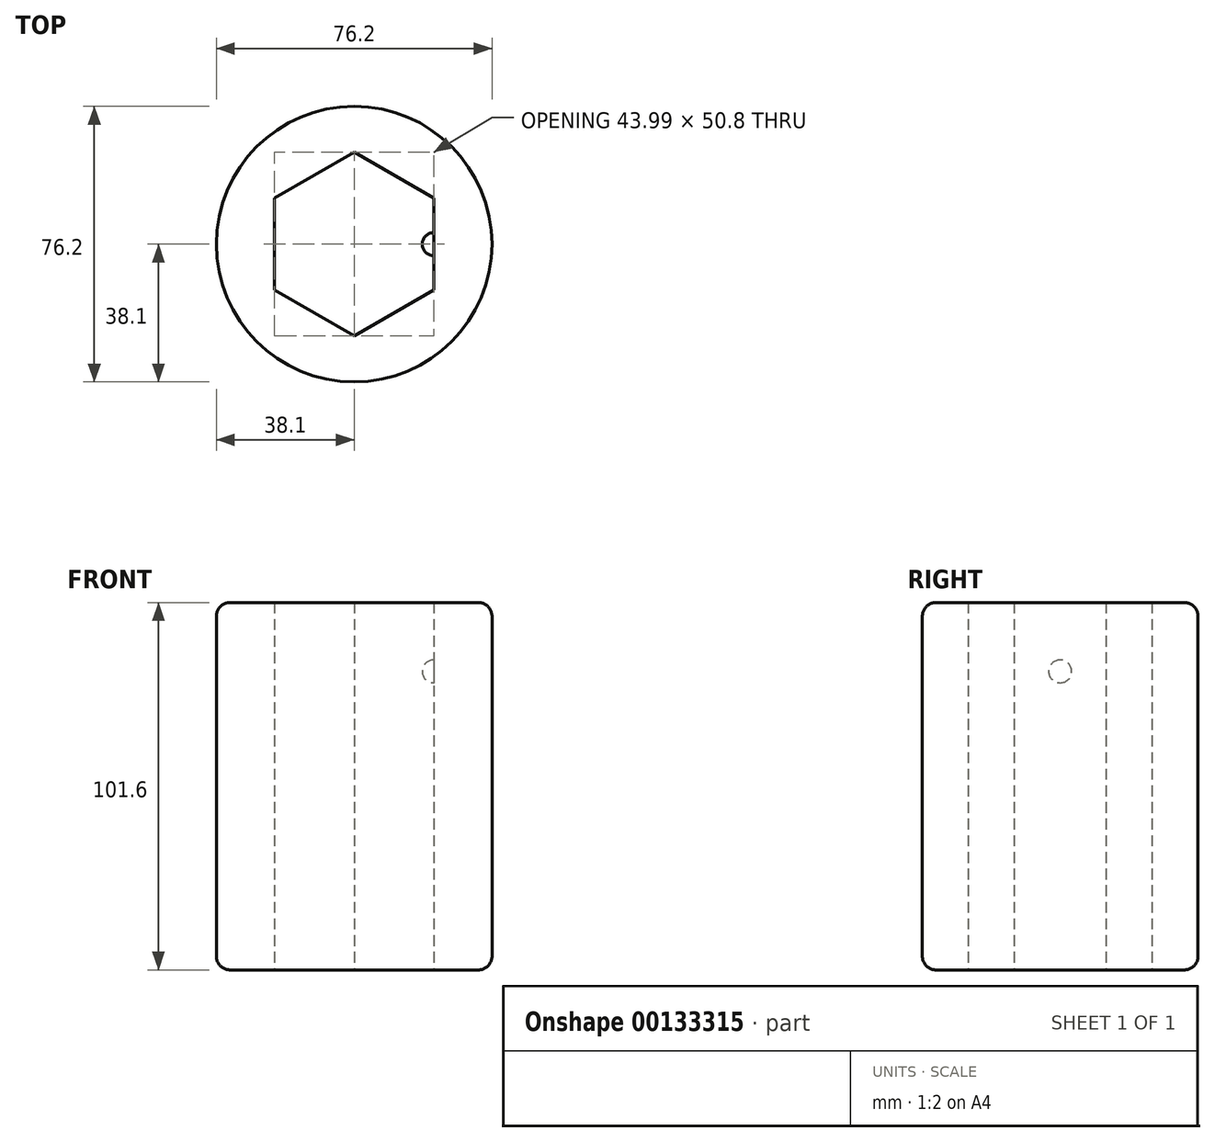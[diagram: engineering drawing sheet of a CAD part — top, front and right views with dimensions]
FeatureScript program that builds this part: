
annotation { "Feature Type Name" : "Feature", "Feature Type Description" : "" }
export const myFeature = defineFeature(function(context is Context, id is Id, definition is map)
    precondition{}
    {
        {
            var Q0;
            Q0=qCreatedBy(makeId("Top.planeOp"),FACE);
            var sketch = newSketch(context, id + "F0", { "sketchPlane" : qUnion([Q0])});
            skCircle(sketch, "E0", {"center": v(0, 0) * mm, "radius": 38.1 * mm});
            skCircle(sketch, "E1.cCircle", {"center": v(0, 0) * mm, "radius": 22 * mm, "construction": true});
            skLineSegment(sketch, "E1.0", {"start": v(0, 25.4) * mm, "end": v(22, 12.7) * mm});
            skLineSegment(sketch, "E1.1", {"start": v(22, 12.7) * mm, "end": v(22, -12.7) * mm});
            skLineSegment(sketch, "E1.2", {"start": v(22, -12.7) * mm, "end": v(0, -25.4) * mm});
            skLineSegment(sketch, "E1.3", {"start": v(0, -25.4) * mm, "end": v(-22, -12.7) * mm});
            skLineSegment(sketch, "E1.4", {"start": v(-22, -12.7) * mm, "end": v(-22, 12.7) * mm});
            skLineSegment(sketch, "E1.5", {"start": v(-22, 12.7) * mm, "end": v(0, 25.4) * mm});
            skPoint(sketch, "E1.0.midPoint", {"position": v(11, 19.05) * mm});
            skSolve(sketch);
        }
        {
            var Q0;
            Q0=makeQuery(id+"F0.imprint","IMPRINT",FACE,{"disambiguationData":[TD([[makeQuery(id+"F0.imprint","IMPRINT",EDGE,{"derivedFrom":sQuery(id+"F0.wireOp",EDGE,"E0")}),1.0]])]});
            extrude(context, id + "F1", {"entities" : qUnion([Q0]), "depth" : 101.6 * mm});
        }
        {
            var Q0;
            Q0=makeQuery(id+"F1.opExtrude","SWEPT_FACE",FACE,{"disambiguationData":[OSD([sQuery(id+"F0.wireOp",EDGE,"E1.1")])]});
            var sketch = newSketch(context, id + "F2", { "sketchPlane" : qUnion([Q0])});
            skArc(sketch, "E2", {"start": v(0, 79.38) * mm, "mid": v(3.18, 82.55) * mm, "end": v(0, 85.73) * mm});
            skPoint(sketch, "E2.centerSnap0", {"position": v(0, 101.6) * mm});
            skLineSegment(sketch, "E3", {"start": v(0, 79.38) * mm, "end": v(0, 85.73) * mm});
            skSolve(sketch);
        }
        {
            var Q0;
            Q0 = qSketchRegion(id + "F2", true);
            var Q1;
            Q1=sQuery(id+"F2.wireOp",EDGE,"E3");
            revolve(context, id + "F3", {"operationType" : NewBodyOperationType.ADD, "entities" : qUnion([Q0]), "axis" : qUnion([Q1]), "revolveType" : RevolveType.FULL});
        }
        {
            var Q0;
            Q0=makeQuery(id+"F1.opExtrude","CAP_EDGE",EDGE,{"disambiguationData":[OSD([sQuery(id+"F0.wireOp",EDGE,"E0")])],"isStart":true});
            var Q1;
            Q1=makeQuery(id+"F1.opExtrude","CAP_EDGE",EDGE,{"disambiguationData":[OSD([sQuery(id+"F0.wireOp",EDGE,"E0")])],"isStart":false});
            fillet(context, id + "F4", {"entities" : qUnion([Q0, Q1]), "radius" : 3.8 * mm, "tangentPropagation" : true, "allowEdgeOverflow" : false});
        }
    });
